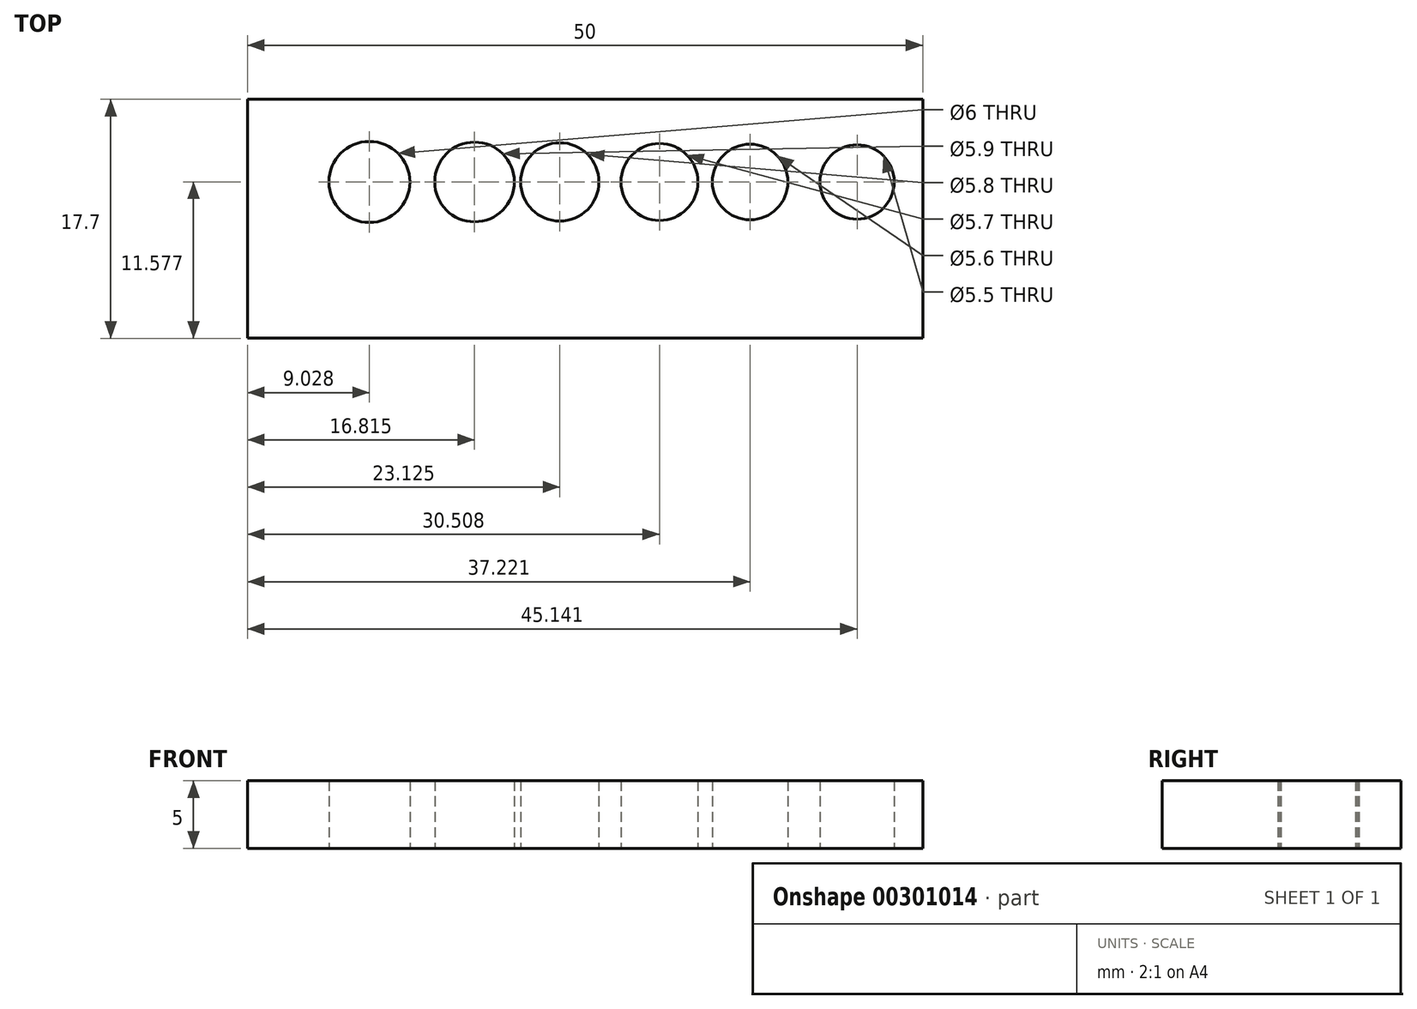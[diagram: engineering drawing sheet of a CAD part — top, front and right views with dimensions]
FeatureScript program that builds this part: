
annotation { "Feature Type Name" : "Feature", "Feature Type Description" : "" }
export const myFeature = defineFeature(function(context is Context, id is Id, definition is map)
    precondition{}
    {
        {
            var Q0;
            Q0=qCreatedBy(makeId("Top.planeOp"),FACE);
            var sketch = newSketch(context, id + "F0", { "sketchPlane" : qUnion([Q0])});
            skLineSegment(sketch, "E0.bottom", {"start": v(-24.9, 8.66) * mm, "end": v(25.1, 8.66) * mm});
            skLineSegment(sketch, "E0.top", {"start": v(-24.9, -9.04) * mm, "end": v(25.1, -9.04) * mm});
            skLineSegment(sketch, "E0.left", {"start": v(-24.9, 8.66) * mm, "end": v(-24.9, -9.04) * mm});
            skLineSegment(sketch, "E0.right", {"start": v(25.1, 8.66) * mm, "end": v(25.1, -9.04) * mm});
            skLineSegment(sketch, "E1", {"start": v(-21.9, 2.54) * mm, "end": v(-15.88, 2.54) * mm, "construction": true});
            skLineSegment(sketch, "E2", {"start": v(-15.88, 2.54) * mm, "end": v(-8.1, 2.54) * mm, "construction": true});
            skLineSegment(sketch, "E3", {"start": v(-8.1, 2.54) * mm, "end": v(-1.79, 2.54) * mm, "construction": true});
            skLineSegment(sketch, "E4", {"start": v(-1.79, 2.54) * mm, "end": v(5.6, 2.54) * mm, "construction": true});
            skLineSegment(sketch, "E5", {"start": v(5.6, 2.54) * mm, "end": v(12.31, 2.54) * mm, "construction": true});
            skLineSegment(sketch, "E6", {"start": v(12.31, 2.54) * mm, "end": v(20.23, 2.54) * mm, "construction": true});
            skSolve(sketch);
        }
        {
            var Q0;
            Q0=makeQuery(id+"F0.imprint","IMPRINT",FACE,{"disambiguationData":[TD([[makeQuery(id+"F0.imprint","IMPRINT",EDGE,{"derivedFrom":sQuery(id+"F0.wireOp",EDGE,"E0.bottom")}),-1.0]])]});
            extrude(context, id + "F1", {"entities" : qUnion([Q0]), "depth" : 5 * mm, "offsetDistance" : 25 * mm});
        }
        {
            var Q0;
            Q0=sQuery(id+"F0.wireOp",VERTEX,"E2.start");
            var Q1;
            Q1=makeQuery(id+"F1.opExtrude","SWEPT_BODY",BODY,{"disambiguationData":[OSD([sQuery(id+"F0.wireOp",EDGE,"E0.bottom"),sQuery(id+"F0.wireOp",EDGE,"E0.top"),sQuery(id+"F0.wireOp",EDGE,"E0.left"),sQuery(id+"F0.wireOp",EDGE,"E0.right")])]});
            hole(context, id + "F2", {"style" : HoleStyle.SIMPLE, "endStyle" : HoleEndStyle.BLIND, "oppositeDirection" : true, "holeDiameter" : 6 * mm, "majorDiameter" : 5 * mm, "holeDepth" : 12 * mm, "isTappedThrough" : true, "tappedDepth" : 12 * mm, "tapClearance" : 3, "locations" : qUnion([Q0]), "scope" : qUnion([Q1])});
        }
        {
            var Q0;
            Q0=sQuery(id+"F0.wireOp",VERTEX,"E3.start");
            var Q1;
            Q1=makeQuery(id+"F1.opExtrude","SWEPT_BODY",BODY,{"disambiguationData":[OSD([sQuery(id+"F0.wireOp",EDGE,"E0.bottom"),sQuery(id+"F0.wireOp",EDGE,"E0.top"),sQuery(id+"F0.wireOp",EDGE,"E0.left"),sQuery(id+"F0.wireOp",EDGE,"E0.right")])]});
            hole(context, id + "F3", {"style" : HoleStyle.SIMPLE, "endStyle" : HoleEndStyle.BLIND, "oppositeDirection" : true, "holeDiameter" : 5.9 * mm, "majorDiameter" : 5 * mm, "holeDepth" : 12 * mm, "isTappedThrough" : true, "tappedDepth" : 12 * mm, "tapClearance" : 3, "locations" : qUnion([Q0]), "scope" : qUnion([Q1])});
        }
        {
            var Q0;
            Q0=sQuery(id+"F0.wireOp",VERTEX,"E4.start");
            var Q1;
            Q1=makeQuery(id+"F1.opExtrude","SWEPT_BODY",BODY,{"disambiguationData":[OSD([sQuery(id+"F0.wireOp",EDGE,"E0.bottom"),sQuery(id+"F0.wireOp",EDGE,"E0.top"),sQuery(id+"F0.wireOp",EDGE,"E0.left"),sQuery(id+"F0.wireOp",EDGE,"E0.right")])]});
            hole(context, id + "F4", {"style" : HoleStyle.SIMPLE, "endStyle" : HoleEndStyle.BLIND, "oppositeDirection" : true, "holeDiameter" : 5.8 * mm, "majorDiameter" : 5 * mm, "holeDepth" : 12 * mm, "isTappedThrough" : true, "tappedDepth" : 12 * mm, "tapClearance" : 3, "locations" : qUnion([Q0]), "scope" : qUnion([Q1])});
        }
        {
            var Q0;
            Q0=sQuery(id+"F0.wireOp",VERTEX,"E4.end");
            var Q1;
            Q1=makeQuery(id+"F1.opExtrude","SWEPT_BODY",BODY,{"disambiguationData":[OSD([sQuery(id+"F0.wireOp",EDGE,"E0.bottom"),sQuery(id+"F0.wireOp",EDGE,"E0.top"),sQuery(id+"F0.wireOp",EDGE,"E0.left"),sQuery(id+"F0.wireOp",EDGE,"E0.right")])]});
            hole(context, id + "F5", {"style" : HoleStyle.SIMPLE, "endStyle" : HoleEndStyle.BLIND, "oppositeDirection" : true, "holeDiameter" : 5.7 * mm, "majorDiameter" : 5 * mm, "holeDepth" : 12 * mm, "isTappedThrough" : true, "tappedDepth" : 12 * mm, "tapClearance" : 3, "locations" : qUnion([Q0]), "scope" : qUnion([Q1])});
        }
        {
            var Q0;
            Q0=sQuery(id+"F0.wireOp",VERTEX,"E5.end");
            var Q1;
            Q1=makeQuery(id+"F1.opExtrude","SWEPT_BODY",BODY,{"disambiguationData":[OSD([sQuery(id+"F0.wireOp",EDGE,"E0.bottom"),sQuery(id+"F0.wireOp",EDGE,"E0.top"),sQuery(id+"F0.wireOp",EDGE,"E0.left"),sQuery(id+"F0.wireOp",EDGE,"E0.right")])]});
            hole(context, id + "F6", {"style" : HoleStyle.SIMPLE, "endStyle" : HoleEndStyle.BLIND, "oppositeDirection" : true, "holeDiameter" : 5.6 * mm, "majorDiameter" : 5 * mm, "holeDepth" : 12 * mm, "isTappedThrough" : true, "tappedDepth" : 12 * mm, "tapClearance" : 3, "locations" : qUnion([Q0]), "scope" : qUnion([Q1])});
        }
        {
            var Q0;
            Q0=sQuery(id+"F0.wireOp",VERTEX,"E6.end");
            var Q1;
            Q1=makeQuery(id+"F1.opExtrude","SWEPT_BODY",BODY,{"disambiguationData":[OSD([sQuery(id+"F0.wireOp",EDGE,"E0.bottom"),sQuery(id+"F0.wireOp",EDGE,"E0.top"),sQuery(id+"F0.wireOp",EDGE,"E0.left"),sQuery(id+"F0.wireOp",EDGE,"E0.right")])]});
            hole(context, id + "F7", {"style" : HoleStyle.SIMPLE, "endStyle" : HoleEndStyle.BLIND, "oppositeDirection" : true, "holeDiameter" : 5.5 * mm, "majorDiameter" : 5 * mm, "holeDepth" : 12 * mm, "isTappedThrough" : true, "tappedDepth" : 12 * mm, "tapClearance" : 3, "locations" : qUnion([Q0]), "scope" : qUnion([Q1])});
        }
    });
